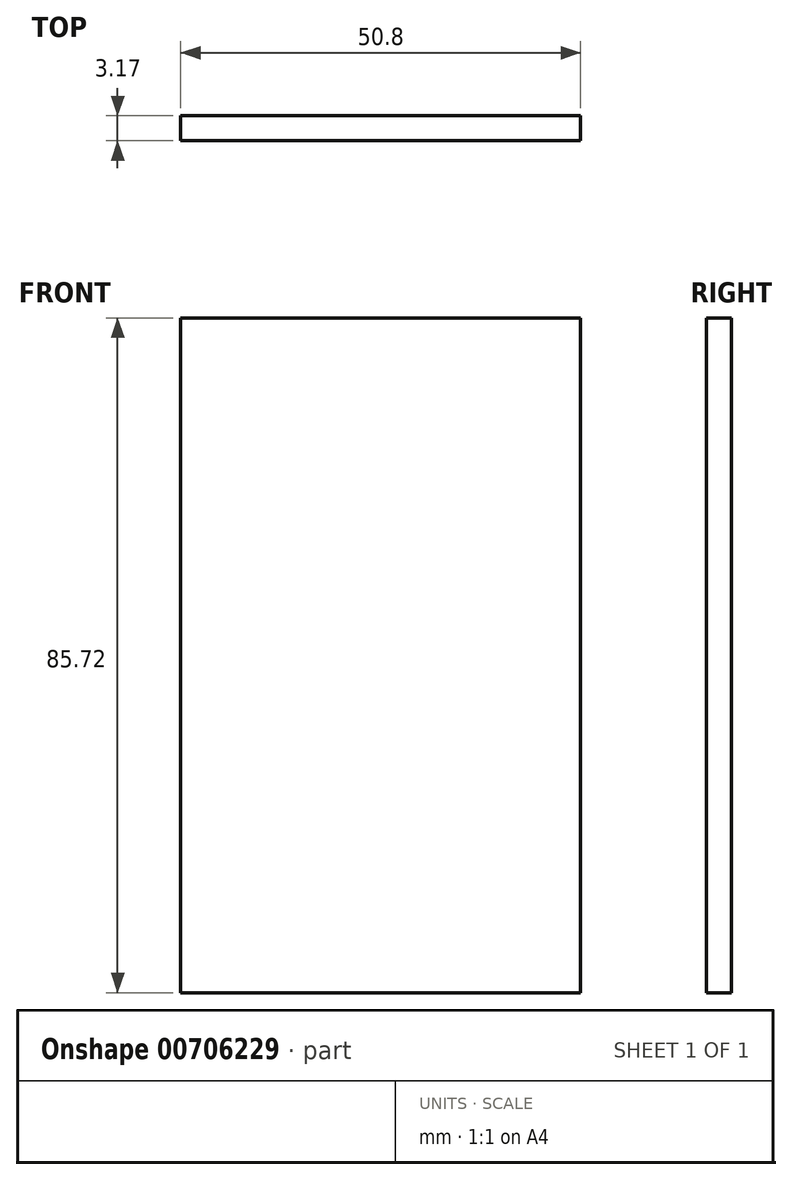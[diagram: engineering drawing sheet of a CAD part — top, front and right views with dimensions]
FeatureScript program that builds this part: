
annotation { "Feature Type Name" : "Feature", "Feature Type Description" : "" }
export const myFeature = defineFeature(function(context is Context, id is Id, definition is map)
    precondition{}
    {
        {
            var Q0;
            Q0=qCreatedBy(makeId("Front.planeOp"),FACE);
            var sketch = newSketch(context, id + "F0", { "sketchPlane" : qUnion([Q0])});
            skLineSegment(sketch, "E0.bottom", {"start": v(-24.5, 54.46) * mm, "end": v(26.3, 54.46) * mm});
            skLineSegment(sketch, "E0.top", {"start": v(-24.5, -31.26) * mm, "end": v(26.3, -31.26) * mm});
            skLineSegment(sketch, "E0.left", {"start": v(-24.5, 54.46) * mm, "end": v(-24.5, -31.26) * mm});
            skLineSegment(sketch, "E0.right", {"start": v(26.3, 54.46) * mm, "end": v(26.3, -31.26) * mm});
            skSolve(sketch);
        }
        {
            var Q0;
            Q0=qSketchRegion(id+"F0",true);
            extrude(context, id + "F1", {"entities" : qUnion([Q0]), "depth" : 3.17 * mm, "offsetDistance" : 25.4 * mm});
        }
    });
